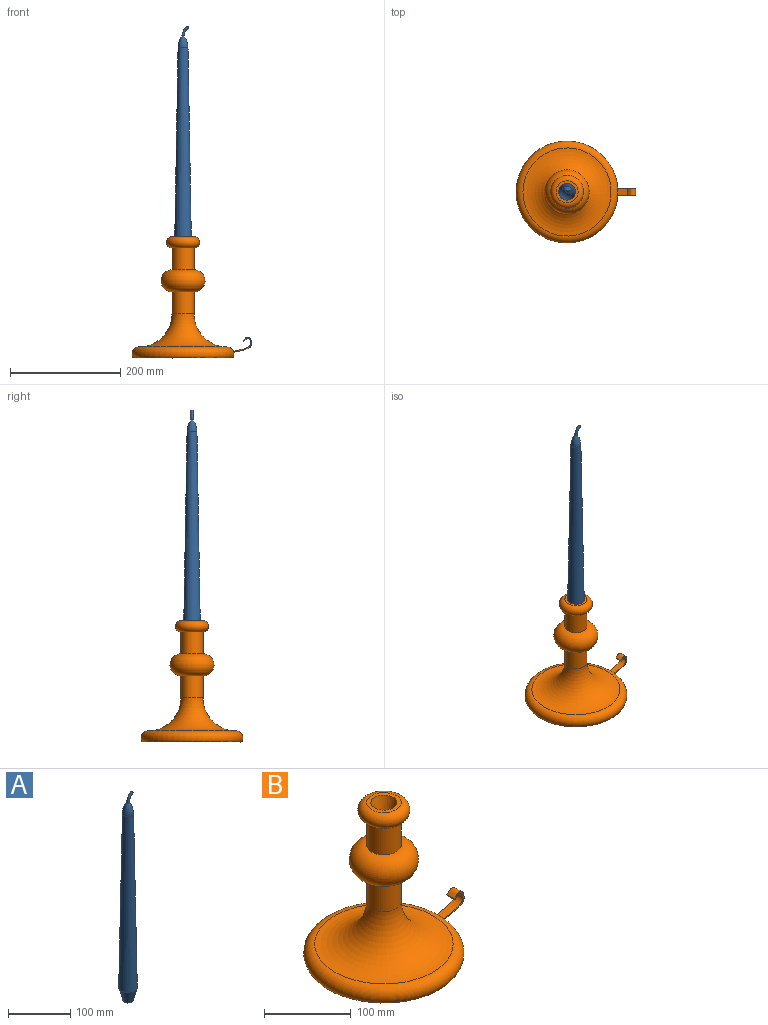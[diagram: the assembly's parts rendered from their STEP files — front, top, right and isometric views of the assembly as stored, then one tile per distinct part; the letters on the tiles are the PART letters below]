
ASSEMBLY  parts=2 mates=1
PART A: 6 faces, bbox 30x30x408 mm
  f0: plane 4x3.48mm, normal (0.87,0,0.49), area 12.6mm2, adj f1
  f1: bspline ~18.01x12.79mm, area 250.6mm2, adj f0,f5
  f2: plane 16.6x16.6mm, normal (0,0,-1), area 216.5mm2, adj f3
  f3: cone r=8.3mm half-angle=15deg, axis (0,0,1), area 1894.6mm2, adj f2,f4
  f4: cone r=15mm half-angle=1deg, axis (0,0,-1), area 25912mm2, adj f3,f5
  f5: revolved ~21.43x18.01mm, area 963.3mm2, adj f1,f4
PART B: 15 faces, bbox 225.6x200.2x221.4 mm
  f0: plane 180x180mm, normal (0,0,-1), area 25446.9mm2, adj f1
  f1: torus R=80mm, axis (0,0,-1), area 15459.9mm2, adj f0,f2,f11,f12,f13,f14
  f2: torus R=80mm, axis (0,0,-1), area 24754.6mm2, adj f1,f3
  f3: cylinder r=20mm len=40mm, axis (0,0,-1), area 5026.5mm2, adj f2,f4
  f4: torus R=20mm, axis (0,0,-1), area 12922.2mm2, adj f3,f5
  f5: cylinder r=20mm len=40mm, axis (0,0,-1), area 5026.5mm2, adj f4,f6
  f6: torus R=20mm, axis (0,0,-1), area 5204.5mm2, adj f5,f7
  f7: plane 40x40mm, normal (0,0,1), area 549.8mm2, adj f6,f8
  f8: cone r=15mm half-angle=15deg, axis (0,0,1), area 1894.6mm2, adj f7,f9
  f9: plane 16.6x16.6mm, normal (0,0,1), area 216.5mm2, adj f8
  f10: plane 12x1.65mm, normal (-0.83,0,-0.56), area 24mm2, adj f11,f12,f13,f14
  f11: plane 34.02x27.63mm, normal (0,1,0), area 120.1mm2, adj f1,f10,f12,f14
  f12: bspline ~35.46x24.26mm, area 693mm2, adj f1,f10,f11,f13
  f13: plane 34.02x27.63mm, normal (0,-1,0), area 120.1mm2, adj f1,f10,f12,f14
  f14: bspline ~37.51x28.24mm, area 773.7mm2, adj f1,f10,f11,f13
PLACE A t=(-1.27,59.45,206.41)mm
PLACE B t=(-1.27,59.45,11.41)mm
MATE fastened B.f8 <-> A.f3  axis (0,0,1) through (-1.27,59.45,206.41)mm
